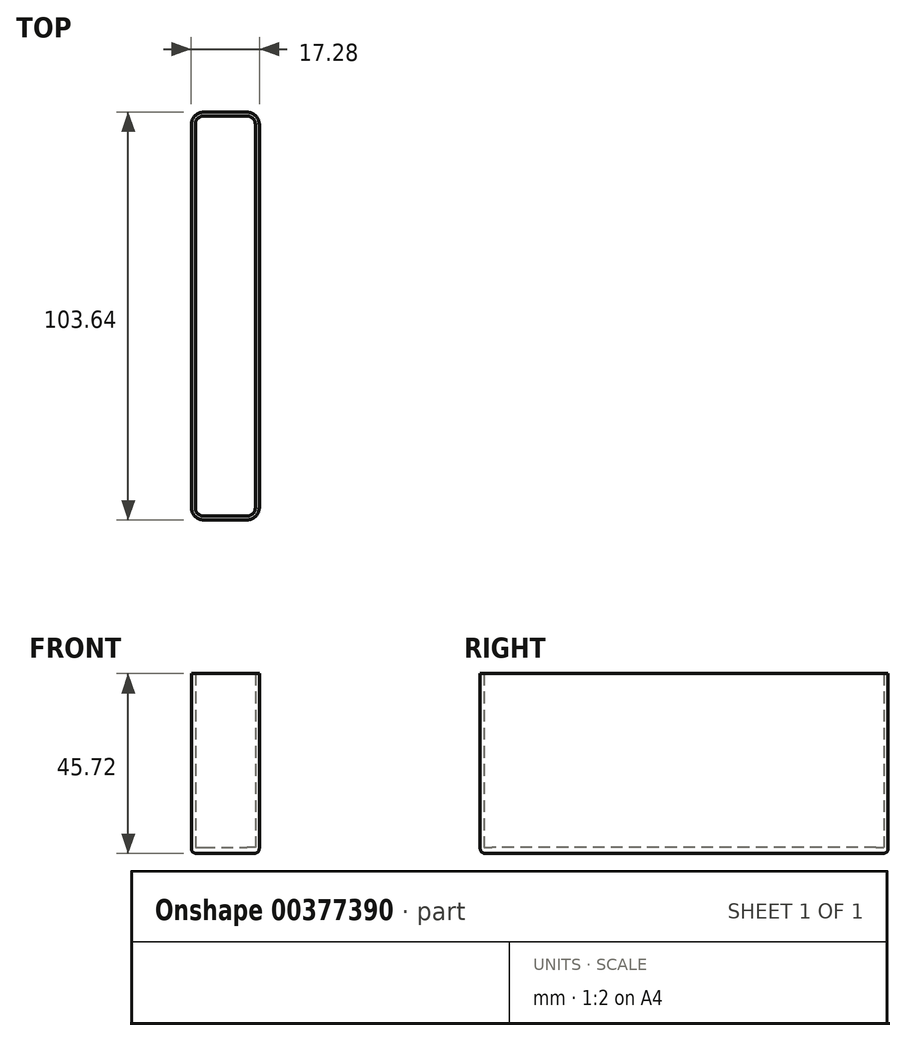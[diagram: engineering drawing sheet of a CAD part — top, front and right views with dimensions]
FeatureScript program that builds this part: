
annotation { "Feature Type Name" : "Feature", "Feature Type Description" : "" }
export const myFeature = defineFeature(function(context is Context, id is Id, definition is map)
    precondition{}
    {
        {
            var Q0;
            Q0=qCreatedBy(makeId("Top.planeOp"),FACE);
            var sketch = newSketch(context, id + "F0", { "sketchPlane" : qUnion([Q0])});
            skLineSegment(sketch, "E0.bottom", {"start": v(-5.46, 51.82) * mm, "end": v(5.46, 51.82) * mm});
            skLineSegment(sketch, "E0.top", {"start": v(-5.46, -51.82) * mm, "end": v(5.46, -51.82) * mm});
            skLineSegment(sketch, "E0.left", {"start": v(-8.64, 48.64) * mm, "end": v(-8.64, -48.64) * mm});
            skLineSegment(sketch, "E0.right", {"start": v(8.64, 48.64) * mm, "end": v(8.64, -48.64) * mm});
            skPoint(sketch, "E0.middle", {"position": v(0, 0) * mm});
            skPoint(sketch, "E1.visualSharp", {"position": v(-8.64, 51.82) * mm});
            skArc(sketch, "E1.filletArc", {"start": v(-5.46, 51.82) * mm, "mid": v(-7.7, 50.89) * mm, "end": v(-8.64, 48.64) * mm});
            skPoint(sketch, "E2.visualSharp", {"position": v(8.64, 51.82) * mm});
            skArc(sketch, "E2.filletArc", {"start": v(8.64, 48.64) * mm, "mid": v(7.7, 50.89) * mm, "end": v(5.46, 51.82) * mm});
            skPoint(sketch, "E3.visualSharp", {"position": v(8.64, -51.82) * mm});
            skArc(sketch, "E3.filletArc", {"start": v(5.46, -51.82) * mm, "mid": v(7.7, -50.89) * mm, "end": v(8.64, -48.64) * mm});
            skPoint(sketch, "E4.visualSharp", {"position": v(-8.64, -51.82) * mm});
            skArc(sketch, "E4.filletArc", {"start": v(-8.64, -48.64) * mm, "mid": v(-7.7, -50.89) * mm, "end": v(-5.46, -51.82) * mm});
            skSolve(sketch);
        }
        {
            var Q0;
            Q0=qSketchRegion(id+"F0",true);
            extrude(context, id + "F1", {"entities" : qUnion([Q0]), "depth" : 1.52 * mm});
        }
        {
            var Q0;
            Q0=makeQuery(id+"F1.opExtrude","CAP_FACE",FACE,{"disambiguationData":[OSD([sQuery(id+"F0.wireOp",EDGE,"E0.bottom"),sQuery(id+"F0.wireOp",EDGE,"E0.top"),sQuery(id+"F0.wireOp",EDGE,"E0.left"),sQuery(id+"F0.wireOp",EDGE,"E0.right")])],"isStart":false});
            var sketch = newSketch(context, id + "F2", { "sketchPlane" : qUnion([Q0])});
            skLineSegment(sketch, "E5.bottom", {"start": v(-5.59, 50.8) * mm, "end": v(5.59, 50.8) * mm});
            skLineSegment(sketch, "E5.top", {"start": v(-5.59, -50.8) * mm, "end": v(5.59, -50.8) * mm});
            skLineSegment(sketch, "E5.left", {"start": v(-7.62, 48.77) * mm, "end": v(-7.62, -48.77) * mm});
            skLineSegment(sketch, "E5.right", {"start": v(7.62, 48.77) * mm, "end": v(7.62, -48.77) * mm});
            skPoint(sketch, "E5.middle", {"position": v(0, 0) * mm});
            skPoint(sketch, "E6.visualSharp", {"position": v(-7.62, 50.8) * mm});
            skArc(sketch, "E6.filletArc", {"start": v(-5.59, 50.8) * mm, "mid": v(-7.02, 50.2) * mm, "end": v(-7.62, 48.77) * mm});
            skPoint(sketch, "E7.visualSharp", {"position": v(7.62, 50.8) * mm});
            skArc(sketch, "E7.filletArc", {"start": v(7.62, 48.77) * mm, "mid": v(7.02, 50.2) * mm, "end": v(5.59, 50.8) * mm});
            skPoint(sketch, "E8.visualSharp", {"position": v(7.62, -50.8) * mm});
            skArc(sketch, "E8.filletArc", {"start": v(5.59, -50.8) * mm, "mid": v(7.02, -50.2) * mm, "end": v(7.62, -48.77) * mm});
            skPoint(sketch, "E9.visualSharp", {"position": v(-7.62, -50.8) * mm});
            skArc(sketch, "E9.filletArc", {"start": v(-7.62, -48.77) * mm, "mid": v(-7.02, -50.2) * mm, "end": v(-5.59, -50.8) * mm});
            skSolve(sketch);
        }
        {
            var Q0;
            Q0=makeQuery(id+"F2.imprint","IMPRINT",FACE,{"disambiguationData":[TD([[makeQuery(id+"F2.imprint","IMPRINT",EDGE,{"derivedFrom":sQuery(id+"F2.wireOp",EDGE,"E5.bottom")}),1.0]])]});
            extrude(context, id + "F3", {"entities" : qUnion([Q0]), "operationType" : NewBodyOperationType.ADD, "depth" : 44.2 * mm});
        }
        {
            var Q0;
            Q0=makeQuery(id+"F1.opExtrude","CAP_FACE",FACE,{"disambiguationData":[OSD([sQuery(id+"F0.wireOp",EDGE,"E0.bottom"),sQuery(id+"F0.wireOp",EDGE,"E0.top"),sQuery(id+"F0.wireOp",EDGE,"E0.left"),sQuery(id+"F0.wireOp",EDGE,"E0.right")])],"isStart":true});
            fillet(context, id + "F4", {"entities" : qUnion([Q0]), "radius" : 1.27 * mm, "tangentPropagation" : true, "allowEdgeOverflow" : false});
        }
    });
